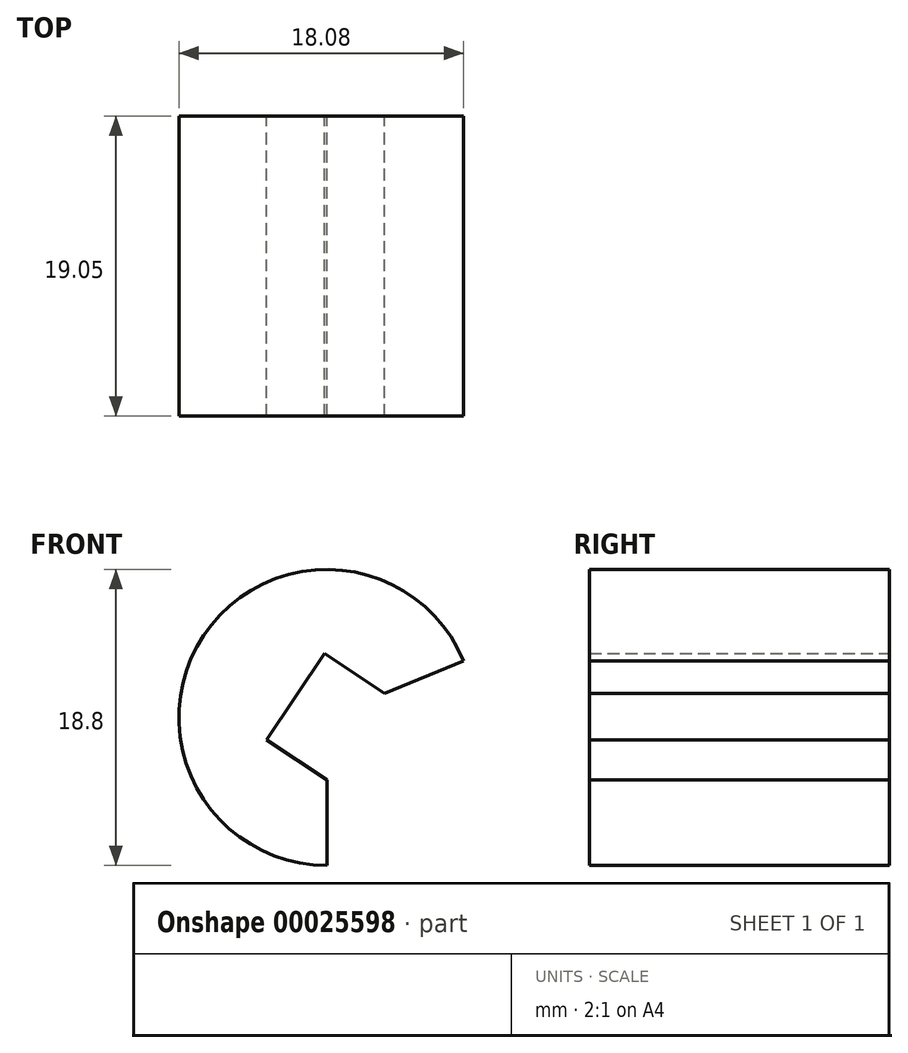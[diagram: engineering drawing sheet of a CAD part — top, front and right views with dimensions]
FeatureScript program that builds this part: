
annotation { "Feature Type Name" : "Feature", "Feature Type Description" : "" }
export const myFeature = defineFeature(function(context is Context, id is Id, definition is map)
    precondition{}
    {
        {
            var Q0;
            Q0=qCreatedBy(makeId("Front.planeOp"),FACE);
            var sketch = newSketch(context, id + "F0", { "sketchPlane" : qUnion([Q0])});
            skArc(sketch, "E0", {"start": v(8.68, 3.6) * mm, "mid": v(-7.81, 5.22) * mm, "end": v(0, -9.4) * mm});
            skLineSegment(sketch, "E1", {"start": v(0, 0) * mm, "end": v(0, -9.4) * mm, "construction": true});
            skLineSegment(sketch, "E2", {"start": v(0, 0) * mm, "end": v(-1.99, 1.33) * mm});
            skLineSegment(sketch, "E3", {"start": v(-1.99, 1.33) * mm, "end": v(-0.15, 4.07) * mm});
            skLineSegment(sketch, "E4.MirrorCS", {"start": v(-1.99, 1.33) * mm, "end": v(-3.82, -1.42) * mm});
            skLineSegment(sketch, "E5", {"start": v(-0.15, 4.07) * mm, "end": v(3.67, 1.52) * mm});
            skLineSegment(sketch, "E6", {"start": v(-3.82, -1.42) * mm, "end": v(0, -3.97) * mm});
            skLineSegment(sketch, "E7", {"start": v(0, 0) * mm, "end": v(0, 0) * mm});
            skLineSegment(sketch, "E8", {"start": v(0, 0) * mm, "end": v(14.35, 5.94) * mm, "construction": true});
            skLineSegment(sketch, "E9", {"start": v(3.67, 1.52) * mm, "end": v(8.68, 3.6) * mm});
            skLineSegment(sketch, "E10", {"start": v(0, -3.97) * mm, "end": v(0, -9.4) * mm});
            skSolve(sketch);
        }
        {
            var Q0;
            Q0=makeQuery(id+"F0.imprint","IMPRINT",FACE,{"disambiguationData":[TD([[makeQuery(id+"F0.imprint","IMPRINT",EDGE,{"derivedFrom":sQuery(id+"F0.wireOp",EDGE,"E0")}),1.0]])]});
            extrude(context, id + "F1", {"entities" : qUnion([Q0]), "depth" : 19.05 * mm});
        }
    });
